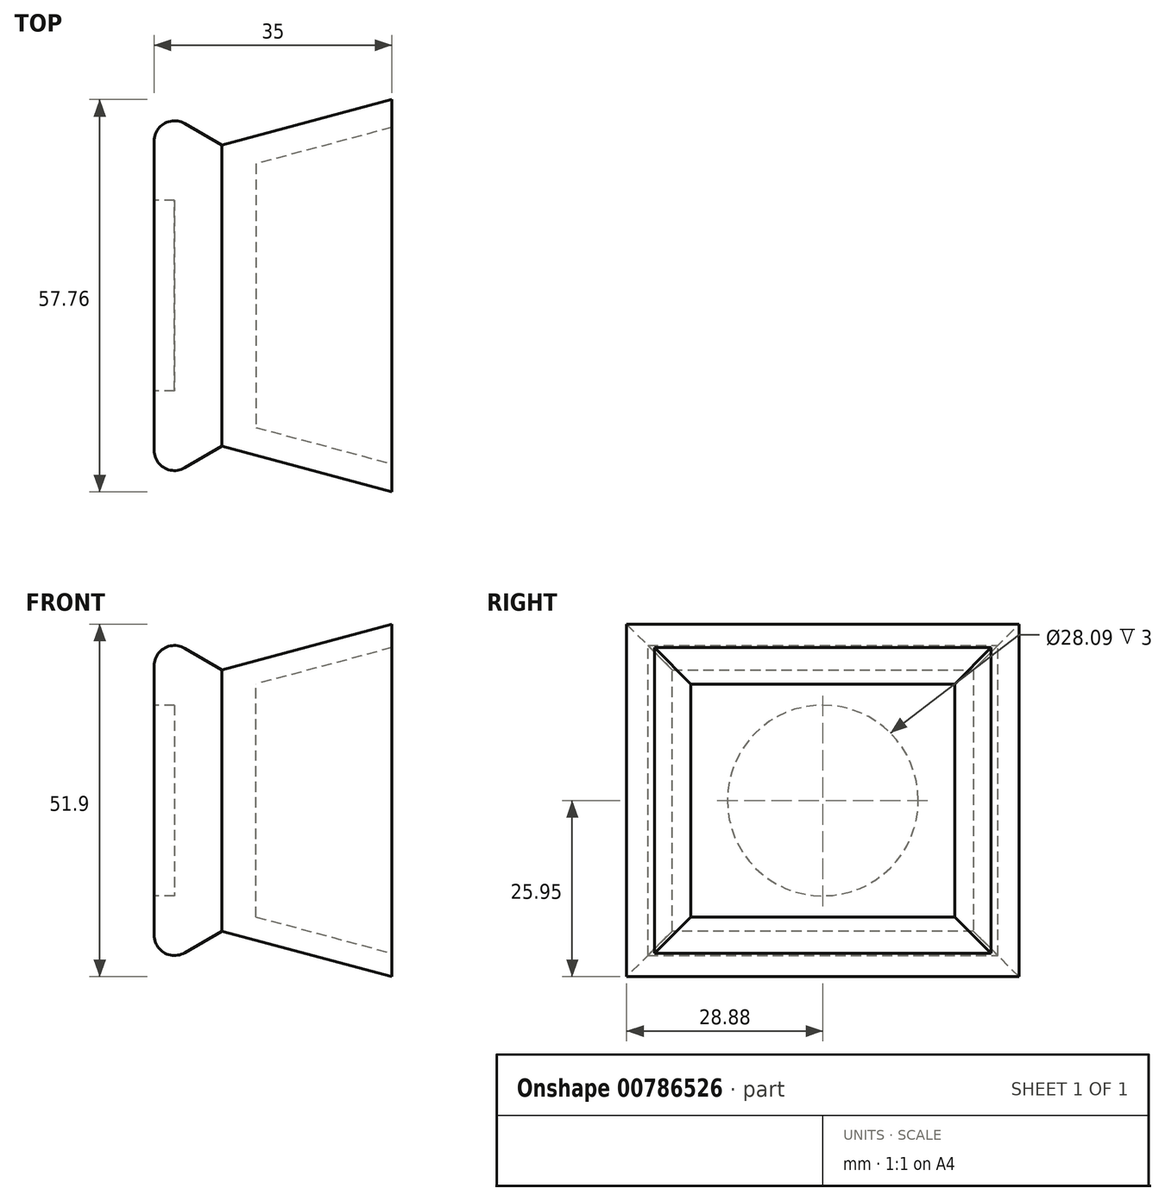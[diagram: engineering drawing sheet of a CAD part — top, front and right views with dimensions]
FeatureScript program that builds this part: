
annotation { "Feature Type Name" : "Feature", "Feature Type Description" : "" }
export const myFeature = defineFeature(function(context is Context, id is Id, definition is map)
    precondition{}
    {
        {
            var Q0;
            Q0=qCreatedBy(makeId("Right.planeOp"),FACE);
            var sketch = newSketch(context, id + "F0", { "sketchPlane" : qUnion([Q0])});
            skLineSegment(sketch, "E0.bottom", {"start": v(22.18, 19.25) * mm, "end": v(-22.18, 19.25) * mm});
            skLineSegment(sketch, "E0.top", {"start": v(22.18, -19.25) * mm, "end": v(-22.18, -19.25) * mm});
            skLineSegment(sketch, "E0.left", {"start": v(22.18, 19.25) * mm, "end": v(22.18, -19.25) * mm});
            skLineSegment(sketch, "E0.right", {"start": v(-22.18, 19.25) * mm, "end": v(-22.18, -19.25) * mm});
            skPoint(sketch, "E0.middle", {"position": v(0, 0) * mm});
            skSolve(sketch);
        }
        {
            var Q0;
            Q0=makeQuery(id+"F0.imprint","IMPRINT",FACE,{"disambiguationData":[TD([[makeQuery(id+"F0.imprint","IMPRINT",EDGE,{"derivedFrom":sQuery(id+"F0.wireOp",EDGE,"E0.bottom")}),1.0]])]});
            extrude(context, id + "F1", {"entities" : qUnion([Q0]), "depth" : 25 * mm, "offsetDistance" : 25 * mm, "hasDraft" : true, "draftAngle" : 15 * degree, "hasSecondDirection" : true, "secondDirectionOppositeDirection" : true, "secondDirectionDepth" : 10 * mm, "hasSecondDirectionDraft" : true, "secondDirectionDraftAngle" : 30 * degree});
        }
        {
            var Q0;
            Q0=makeQuery(id+"F1.opExtrude","CAP_FACE",FACE,{"disambiguationData":[OSD([sQuery(id+"F0.wireOp",EDGE,"E0.bottom"),sQuery(id+"F0.wireOp",EDGE,"E0.top"),sQuery(id+"F0.wireOp",EDGE,"E0.left"),sQuery(id+"F0.wireOp",EDGE,"E0.right")])],"isStart":false});
            var sketch = newSketch(context, id + "F2", { "sketchPlane" : qUnion([Q0])});
            skLineSegment(sketch, "E1.bottom", {"start": v(24.77, 22.5) * mm, "end": v(-24.77, 22.5) * mm});
            skLineSegment(sketch, "E1.top", {"start": v(24.77, -22.5) * mm, "end": v(-24.77, -22.5) * mm});
            skLineSegment(sketch, "E1.left", {"start": v(24.77, 22.5) * mm, "end": v(24.77, -22.5) * mm});
            skLineSegment(sketch, "E1.right", {"start": v(-24.77, 22.5) * mm, "end": v(-24.77, -22.5) * mm});
            skPoint(sketch, "E1.middle", {"position": v(0, 0) * mm});
            skSolve(sketch);
        }
        {
            var Q0;
            Q0=makeQuery(id+"F2.imprint","IMPRINT",FACE,{"disambiguationData":[TD([[makeQuery(id+"F2.imprint","IMPRINT",EDGE,{"derivedFrom":sQuery(id+"F2.wireOp",EDGE,"E1.bottom")}),1.0]])]});
            extrude(context, id + "F3", {"entities" : qUnion([Q0]), "operationType" : NewBodyOperationType.REMOVE, "oppositeDirection" : true, "depth" : 20 * mm, "offsetDistance" : 25 * mm, "hasDraft" : true, "draftAngle" : 15 * degree, "draftPullDirection" : true});
        }
        {
            var Q0;
            Q0=makeQuery(id+"F1.opExtrude","CAP_EDGE",EDGE,{"disambiguationData":[OSD([sQuery(id+"F0.wireOp",EDGE,"E0.bottom")])],"isStart":true});
            var Q1;
            Q1=makeQuery(id+"F1.opExtrude","CAP_EDGE",EDGE,{"disambiguationData":[OSD([sQuery(id+"F0.wireOp",EDGE,"E0.right")])],"isStart":true});
            var Q2;
            Q2=makeQuery(id+"F1.opExtrude","CAP_EDGE",EDGE,{"disambiguationData":[OSD([sQuery(id+"F0.wireOp",EDGE,"E0.top")])],"isStart":true});
            var Q3;
            Q3=makeQuery(id+"F1.opExtrude","CAP_EDGE",EDGE,{"disambiguationData":[OSD([sQuery(id+"F0.wireOp",EDGE,"E0.left")])],"isStart":true});
            fillet(context, id + "F4", {"entities" : qUnion([Q0, Q1, Q2, Q3]), "radius" : 3 * mm, "tangentPropagation" : true, "allowEdgeOverflow" : false});
        }
        {
            var Q0;
            Q0=makeQuery(id+"F1.opExtrude","CAP_FACE",FACE,{"disambiguationData":[OSD([sQuery(id+"F0.wireOp",EDGE,"E0.bottom"),sQuery(id+"F0.wireOp",EDGE,"E0.top"),sQuery(id+"F0.wireOp",EDGE,"E0.left"),sQuery(id+"F0.wireOp",EDGE,"E0.right")])],"isStart":true});
            var sketch = newSketch(context, id + "F5", { "sketchPlane" : qUnion([Q0])});
            skCircle(sketch, "E2", {"center": v(0, 0) * mm, "radius": 14.04 * mm});
            skSolve(sketch);
        }
        {
            var Q0;
            Q0=makeQuery(id+"F5.imprint","IMPRINT",FACE,{"disambiguationData":[TD([[makeQuery(id+"F5.imprint","IMPRINT",EDGE,{"derivedFrom":sQuery(id+"F5.wireOp",EDGE,"E2")}),1.0]])]});
            extrude(context, id + "F6", {"entities" : qUnion([Q0]), "operationType" : NewBodyOperationType.REMOVE, "oppositeDirection" : true, "depth" : 3 * mm, "offsetDistance" : 25 * mm});
        }
    });
